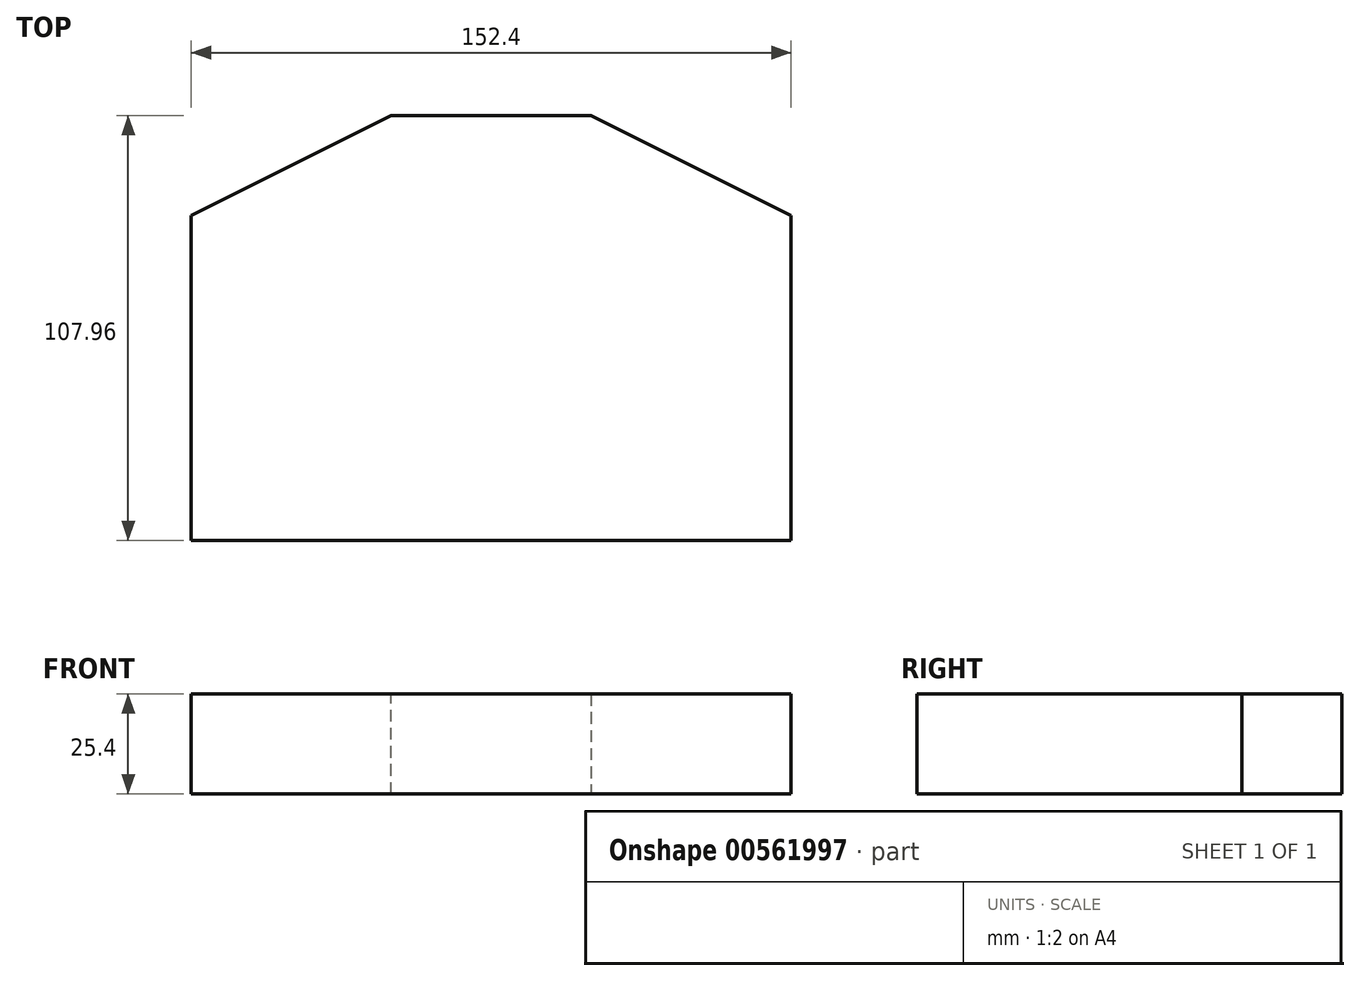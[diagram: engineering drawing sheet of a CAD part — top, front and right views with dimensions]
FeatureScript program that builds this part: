
annotation { "Feature Type Name" : "Feature", "Feature Type Description" : "" }
export const myFeature = defineFeature(function(context is Context, id is Id, definition is map)
    precondition{}
    {
        {
            var Q0;
            Q0=qCreatedBy(makeId("Top.planeOp"),FACE);
            var sketch = newSketch(context, id + "F0", { "sketchPlane" : qUnion([Q0])});
            skLineSegment(sketch, "E0.bottom", {"start": v(76.2, -53.98) * mm, "end": v(-76.2, -53.98) * mm});
            skLineSegment(sketch, "E0.top", {"start": v(76.2, 53.98) * mm, "end": v(-76.2, 53.98) * mm});
            skLineSegment(sketch, "E0.left", {"start": v(76.2, -53.98) * mm, "end": v(76.2, 53.97) * mm});
            skLineSegment(sketch, "E0.right", {"start": v(-76.2, -53.98) * mm, "end": v(-76.2, 53.97) * mm});
            skPoint(sketch, "E0.middle", {"position": v(0, 0) * mm});
            skSolve(sketch);
        }
        {
            var Q0;
            Q0 = qSketchRegion(id + "F0", true);
            extrude(context, id + "F1", {"entities" : qUnion([Q0]), "depth" : 25.4 * mm, "offsetDistance" : 25.4 * mm});
        }
        {
            var Q0;
            Q0=makeQuery(id+"F1.opExtrude","SWEPT_EDGE",EDGE,{"disambiguationData":[OSD([sQuery(id+"F0.wireOp",EDGE,"E0.top"),sQuery(id+"F0.wireOp",EDGE,"E0.right")])]});
            var Q1;
            Q1=makeQuery(id+"F1.opExtrude","SWEPT_EDGE",EDGE,{"disambiguationData":[OSD([sQuery(id+"F0.wireOp",EDGE,"E0.top"),sQuery(id+"F0.wireOp",EDGE,"E0.left")])]});
            chamfer(context, id + "F2", {"entities" : qUnion([Q0, Q1]), "chamferType" : ChamferType.TWO_OFFSETS, "width1" : 25.4 * mm, "oppositeDirection" : false, "width2" : 50.8 * mm, "tangentPropagation" : true});
        }
    });
